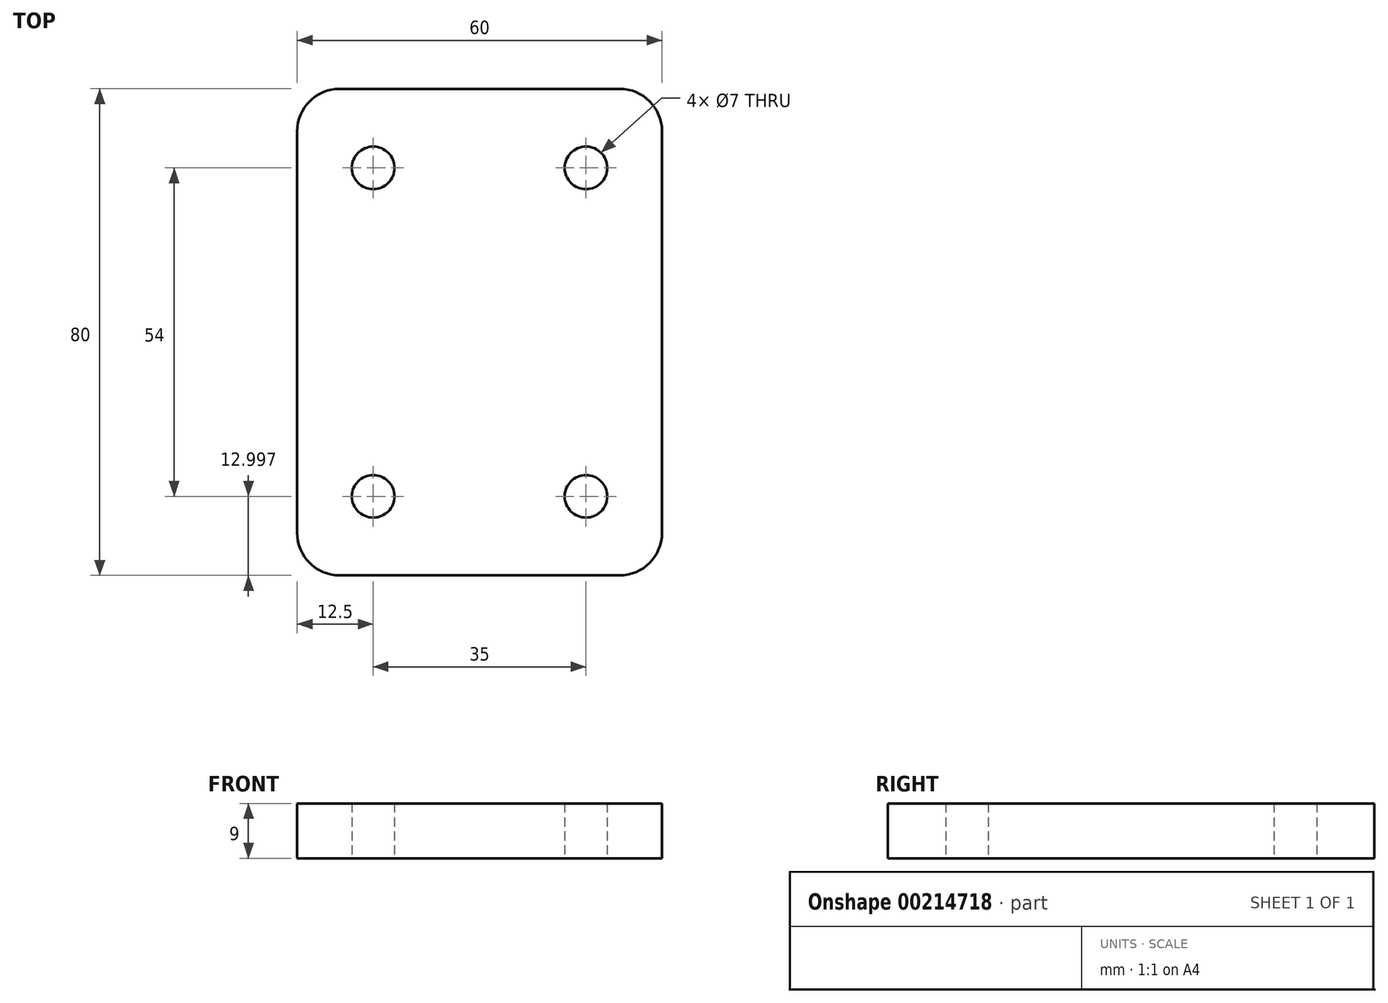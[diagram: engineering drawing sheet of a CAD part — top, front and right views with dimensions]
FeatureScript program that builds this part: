
annotation { "Feature Type Name" : "Feature", "Feature Type Description" : "" }
export const myFeature = defineFeature(function(context is Context, id is Id, definition is map)
    precondition{}
    {
        {
            var Q0;
            Q0=qCreatedBy(makeId("Top.planeOp"),FACE);
            var sketch = newSketch(context, id + "F0", { "sketchPlane" : qUnion([Q0])});
            skLineSegment(sketch, "E0.bottom", {"start": v(-63.75, -3.76) * mm, "end": v(-17.75, -3.76) * mm});
            skLineSegment(sketch, "E0.top", {"start": v(-63.75, -83.76) * mm, "end": v(-17.75, -83.76) * mm});
            skLineSegment(sketch, "E0.left", {"start": v(-70.75, -10.76) * mm, "end": v(-70.75, -76.76) * mm});
            skLineSegment(sketch, "E0.right", {"start": v(-10.75, -10.76) * mm, "end": v(-10.75, -76.76) * mm});
            skPoint(sketch, "E1.visualSharp", {"position": v(-70.75, -3.76) * mm});
            skArc(sketch, "E1.filletArc", {"start": v(-63.75, -3.76) * mm, "mid": v(-68.7, -5.81) * mm, "end": v(-70.75, -10.76) * mm});
            skPoint(sketch, "E2.visualSharp", {"position": v(-10.75, -3.76) * mm});
            skArc(sketch, "E2.filletArc", {"start": v(-10.75, -10.76) * mm, "mid": v(-12.8, -5.81) * mm, "end": v(-17.75, -3.76) * mm});
            skPoint(sketch, "E3.visualSharp", {"position": v(-10.75, -83.76) * mm});
            skArc(sketch, "E3.filletArc", {"start": v(-17.75, -83.76) * mm, "mid": v(-12.8, -81.71) * mm, "end": v(-10.75, -76.76) * mm});
            skPoint(sketch, "E4.visualSharp", {"position": v(-70.75, -83.76) * mm});
            skArc(sketch, "E4.filletArc", {"start": v(-70.75, -76.76) * mm, "mid": v(-68.7, -81.71) * mm, "end": v(-63.75, -83.76) * mm});
            skCircle(sketch, "E5", {"center": v(-58.25, -16.76) * mm, "radius": 3.5 * mm});
            skCircle(sketch, "E6", {"center": v(-23.25, -16.76) * mm, "radius": 3.5 * mm});
            skCircle(sketch, "E7", {"center": v(-23.25, -70.76) * mm, "radius": 3.5 * mm});
            skCircle(sketch, "E8", {"center": v(-58.25, -70.76) * mm, "radius": 3.5 * mm});
            skSolve(sketch);
        }
        {
            var Q0;
            Q0=makeQuery(id+"F0.imprint","IMPRINT",FACE,{"disambiguationData":[TD([[makeQuery(id+"F0.imprint","IMPRINT",EDGE,{"derivedFrom":sQuery(id+"F0.wireOp",EDGE,"E0.bottom")}),-1.0]])]});
            extrude(context, id + "F1", {"entities" : qUnion([Q0]), "depth" : 9 * mm});
        }
    });
